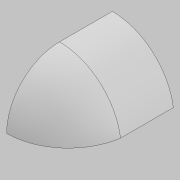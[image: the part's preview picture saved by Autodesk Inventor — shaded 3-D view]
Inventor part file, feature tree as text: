
AUTODESK INVENTOR PART (.ipt)
format: ipt  version: 2021 (Build 250183000, 183)  size: 133,120 bytes
history: native  units: mm
features: sketch x3, other x2, extrude x2, revolve x1
ambient origin geometry x8: Origin, YZ Plane, XZ Plane, XY Plane, X Axis, Y Axis, Z Axis, Center Point
bodies: Body1 (feature_tree)
feature tree (8):
  revolve  "Revolution2"  [1 undecoded]
  other  "end1"
  extrude  "Extrusion1"  Depth=150.0mm
  other  "end2"
  extrude  "Extrusion2"  Depth=10.0mm
  sketch  "Sketch1"  dims[d0=0.0mm d1=0.0mm]
  sketch  "Sketch3"  dims[d2=0.0mm d3=150.0mm]
  sketch  "Sketch4"  dims[d6=900.0mm d8=1039.230485mm d10=0.0mm d11=10.0mm d12=0.0mm d13=90.0deg d14=1039.230485mm d15=0.0mm d16=900.0mm d17=0.0mm d9=0.872665mm]
note: 1 required parameter value undecoded (feature->parameter linkage not recoverable at this tier; creation-order binding heuristic only, values carry confidence <= 0.55)
